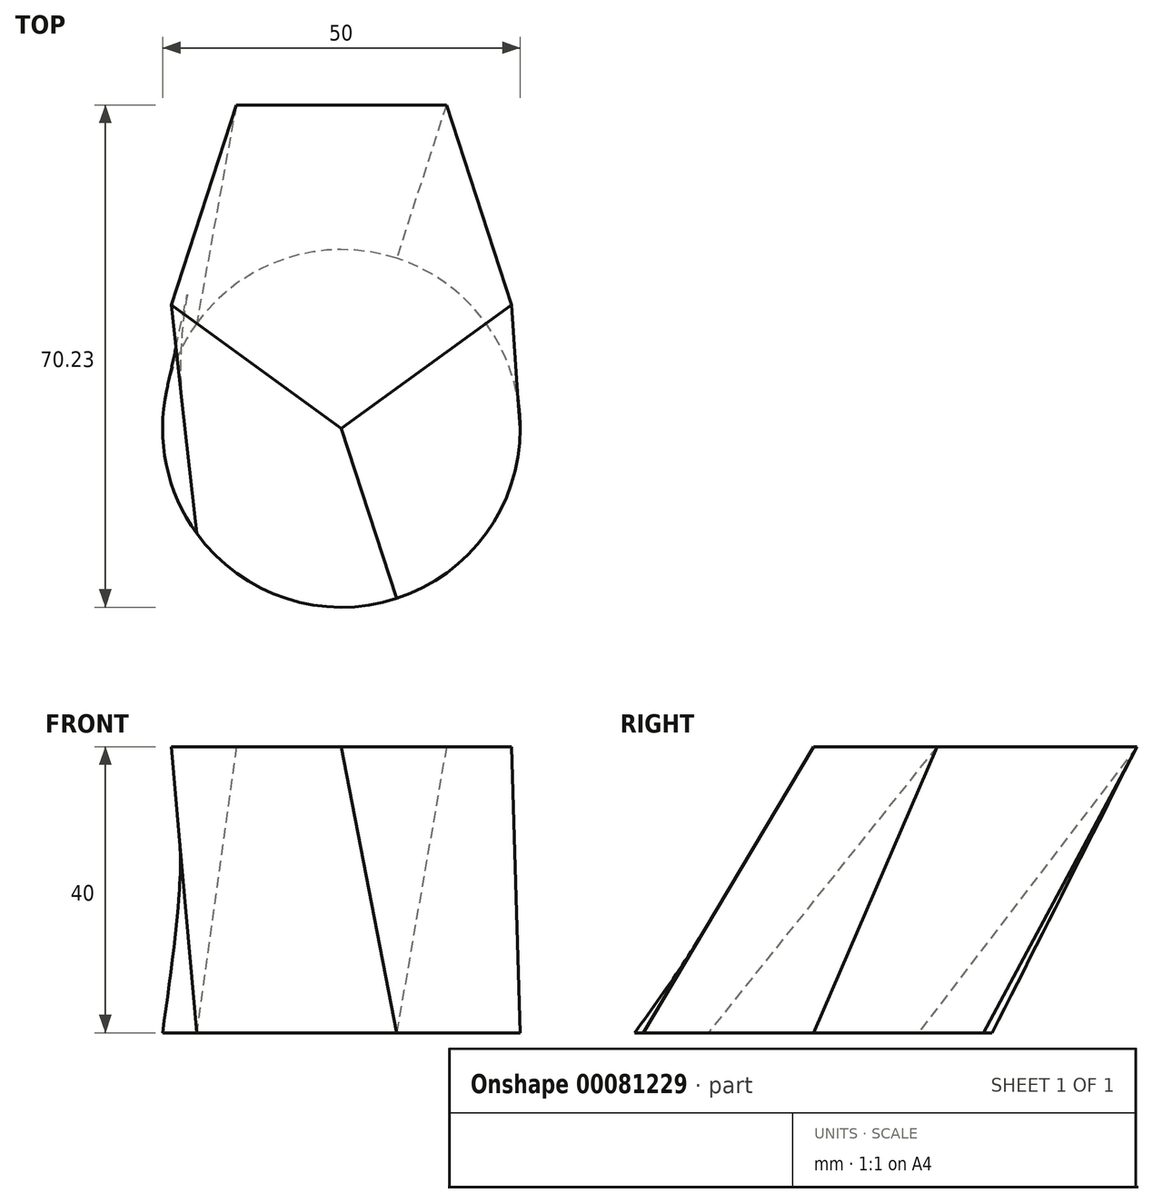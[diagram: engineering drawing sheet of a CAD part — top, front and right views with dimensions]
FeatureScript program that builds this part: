
annotation { "Feature Type Name" : "Feature", "Feature Type Description" : "" }
export const myFeature = defineFeature(function(context is Context, id is Id, definition is map)
    precondition{}
    {
        {
            var Q0;
            Q0=qCreatedBy(makeId("Top.planeOp"),FACE);
            var sketch = newSketch(context, id + "F0", { "sketchPlane" : qUnion([Q0])});
            skCircle(sketch, "E0", {"center": v(0, 0) * mm, "radius": 25 * mm});
            skSolve(sketch);
        }
        {
            var Q0;
            Q0=qCreatedBy(makeId("Top.planeOp"),FACE);
            cPlane(context, id + "F1", {"entities" : qUnion([Q0]), "cplaneType" : CPlaneType.OFFSET, "offset" : 40 * mm, "width" : 150 * mm, "height" : 150 * mm});
        }
        {
            var Q0;
            Q0=qCreatedBy(id+"F1.planeOp",FACE);
            var sketch = newSketch(context, id + "F2", { "sketchPlane" : qUnion([Q0])});
            skCircle(sketch, "E1.cCircle", {"center": v(0, 25) * mm, "radius": 20.23 * mm, "construction": true});
            skLineSegment(sketch, "E1.0", {"start": v(14.7, 45.23) * mm, "end": v(23.78, 17.27) * mm});
            skLineSegment(sketch, "E1.1", {"start": v(23.78, 17.27) * mm, "end": v(0, 0) * mm});
            skLineSegment(sketch, "E1.2", {"start": v(0, 0) * mm, "end": v(-23.78, 17.27) * mm});
            skLineSegment(sketch, "E1.3", {"start": v(-23.78, 17.27) * mm, "end": v(-14.7, 45.23) * mm});
            skLineSegment(sketch, "E1.4", {"start": v(-14.7, 45.23) * mm, "end": v(14.7, 45.23) * mm});
            skPoint(sketch, "E1.0.midPoint", {"position": v(19.24, 31.25) * mm});
            skCircle(sketch, "E2.cCircle", {"center": v(0, -25) * mm, "radius": 20.23 * mm, "construction": true});
            skLineSegment(sketch, "E2.0", {"start": v(0, 0) * mm, "end": v(23.78, -17.27) * mm});
            skLineSegment(sketch, "E2.1", {"start": v(23.78, -17.27) * mm, "end": v(14.7, -45.23) * mm});
            skLineSegment(sketch, "E2.2", {"start": v(14.7, -45.23) * mm, "end": v(-14.7, -45.23) * mm});
            skLineSegment(sketch, "E2.3", {"start": v(-14.7, -45.23) * mm, "end": v(-23.78, -17.27) * mm});
            skLineSegment(sketch, "E2.4", {"start": v(-23.78, -17.27) * mm, "end": v(0, 0) * mm});
            skPoint(sketch, "E2.0.midPoint", {"position": v(11.89, -8.64) * mm});
            skSolve(sketch);
        }
        {
            var Q0;
            Q0=makeQuery(id+"F0.imprint","IMPRINT",FACE,{"disambiguationData":[TD([[makeQuery(id+"F0.imprint","IMPRINT",EDGE,{"derivedFrom":sQuery(id+"F0.wireOp",EDGE,"E0")}),1.0]])]});
            var Q1;
            Q1=makeQuery(id+"F2.imprint","IMPRINT",FACE,{"disambiguationData":[TD([[makeQuery(id+"F2.imprint","IMPRINT",EDGE,{"derivedFrom":sQuery(id+"F2.wireOp",EDGE,"E2.0")}),-1.0]])]});
            loft(context, id + "F3", {"bodyType" : ToolBodyType.SURFACE, "wireProfilesArray" : [{ "wireProfileEntities" : qUnion([Q0]) }, { "wireProfileEntities" : qUnion([Q1]) }]});
        }
        {
            var Q0;
            Q0=makeQuery(id+"F2.imprint","IMPRINT",FACE,{"disambiguationData":[TD([[makeQuery(id+"F2.imprint","IMPRINT",EDGE,{"derivedFrom":sQuery(id+"F2.wireOp",EDGE,"E1.0")}),-1.0]])]});
            var Q1;
            Q1=makeQuery(id+"F0.imprint","IMPRINT",FACE,{"disambiguationData":[TD([[makeQuery(id+"F0.imprint","IMPRINT",EDGE,{"derivedFrom":sQuery(id+"F0.wireOp",EDGE,"E0")}),1.0]])]});
            loft(context, id + "F4", {"sheetProfilesArray" : [{ "sheetProfileEntities" : qUnion([Q0]) }, { "sheetProfileEntities" : qUnion([Q1]) }]});
        }
    });
